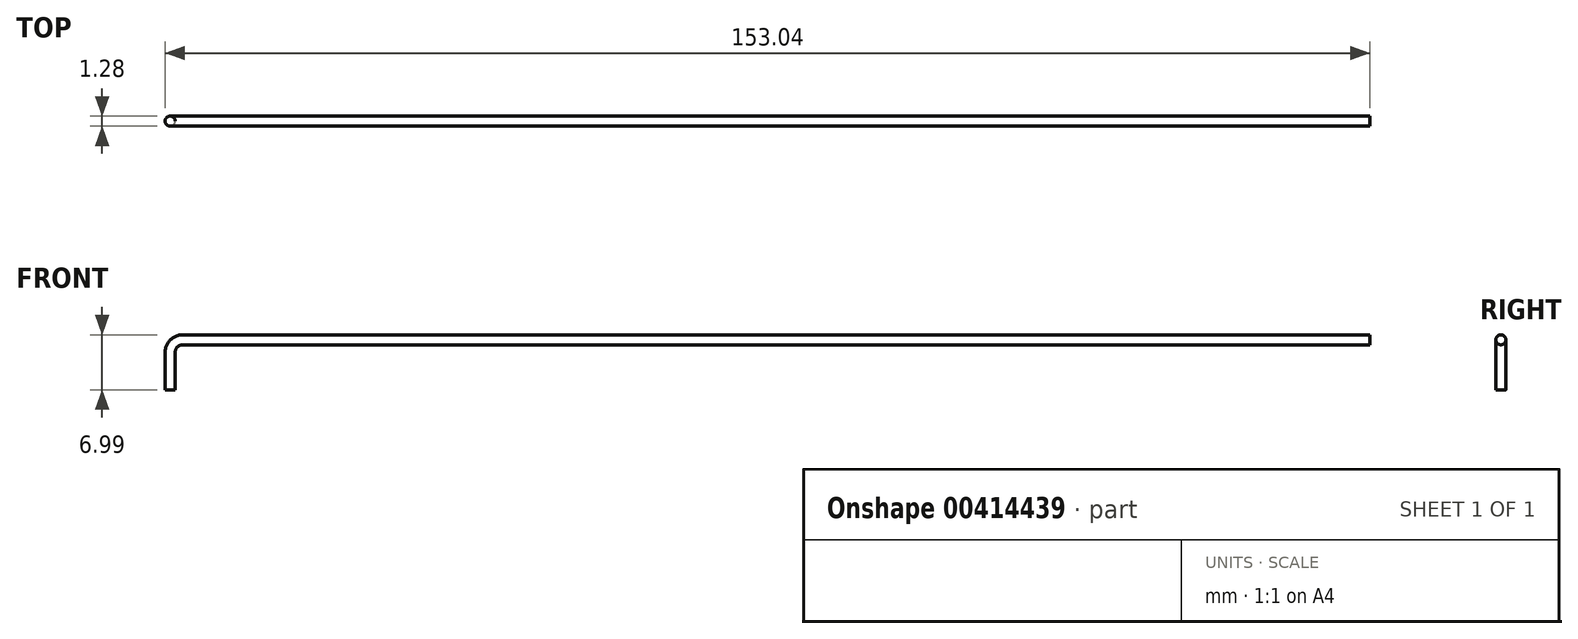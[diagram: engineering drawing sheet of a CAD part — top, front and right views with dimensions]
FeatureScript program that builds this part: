
annotation { "Feature Type Name" : "Feature", "Feature Type Description" : "" }
export const myFeature = defineFeature(function(context is Context, id is Id, definition is map)
    precondition{}
    {
        {
            var Q0;
            Q0=qCreatedBy(makeId("Front.planeOp"),FACE);
            var sketch = newSketch(context, id + "F0", { "sketchPlane" : qUnion([Q0])});
            skLineSegment(sketch, "E0", {"start": v(0, 0) * mm, "end": v(0, 4.76) * mm});
            skLineSegment(sketch, "E1", {"start": v(1.59, 6.35) * mm, "end": v(152.4, 6.35) * mm});
            skPoint(sketch, "E2.visualSharp", {"position": v(0, 6.35) * mm});
            skArc(sketch, "E2.filletArc", {"start": v(1.59, 6.35) * mm, "mid": v(0.46, 5.89) * mm, "end": v(0, 4.76) * mm});
            skSolve(sketch);
        }
        {
            var Q0;
            Q0=qCreatedBy(makeId("Top.planeOp"),FACE);
            var sketch = newSketch(context, id + "F1", { "sketchPlane" : qUnion([Q0])});
            skCircle(sketch, "E3", {"center": v(0, 0) * mm, "radius": 0.64 * mm});
            skSolve(sketch);
        }
        {
            var Q0;
            Q0 = qSketchRegion(id + "F1", true);
            var Q1;
            Q1 = qConstructionFilter(qBodyType(qCreatedBy(id + "F0" ,EDGE), BodyType.WIRE), ConstructionObject.NO);
            sweep(context, id + "F2", {"profiles" : qUnion([Q0]), "path" : qUnion([Q1])});
        }
    });
